# Revit family: FP-Revit20-en-OS76NDTDX1-Oven-0-90003707A-AU-NZ
name_source: partatom
category: Specialty Equipment
units: mm (PartAtom-declared; Revit-internal decimal feet)

## family parameters
Always vertical = Yes
Cut with Voids When Loaded = Yes
Part Type = Normal
Room Calculation Point = No
Round Connector Dimension = Use Diameter
Shared = No
Work Plane-Based = No

## types (1)
- OS76NDTDX1 (Stainless steel)
    Cavity - Depth = 570 mm  [stored 1.87008 ft]
    Cavity - Height = 440 mm  [stored 1.44357 ft]
    Cavity - Width = 724 mm  [stored 2.37533 ft]
    Chassis - Depth = 545 mm  [stored 1.78806 ft]
    Chassis - Height = 435 mm  [stored 1.42717 ft]
    Chassis - Width = 720 mm  [stored 2.3622 ft]
    Connector Description = 208 or 240 V, 60 Hz, 20A
    Default Elevation = 0 mm  [stored 0 ft]
    Description = Combination Steam Oven, 76cm
    Manufacturer = Fisher & Paykel Appliances
    Material - Chassis = Fisher & Paykel - Aluminium
    Material - Clearance = Fisher & Paykel - Clearance Required (Cutout)
    Material - Dial = Fisher & Paykel - Stainless Steel
    Material - Door Clearance = Fisher & Paykel - Clearance Required
    Material - Glass = Fisher & Paykel - Glass, Black
    Material - Handle = Fisher & Paykel - Stainless Steel
    Material - Trim = Fisher & Paykel - Stainless Steel
    Model = OS76NDTDX1
    Product - Depth (excluding handles and dials) = 565 mm  [stored 1.85367 ft]
    Product - Width = 760 mm  [stored 2.49344 ft]
    Product -Height = 458 mm  [stored 1.50262 ft]
    URL = www.fisherpaykel.com

note: [stored X ft] marks values corroborated as IEEE doubles in the binary element streams (Revit-internal decimal feet)

## geometry (parser evidence)
native form markers: Sweep x15
no freeform markers — native parametric forms only
